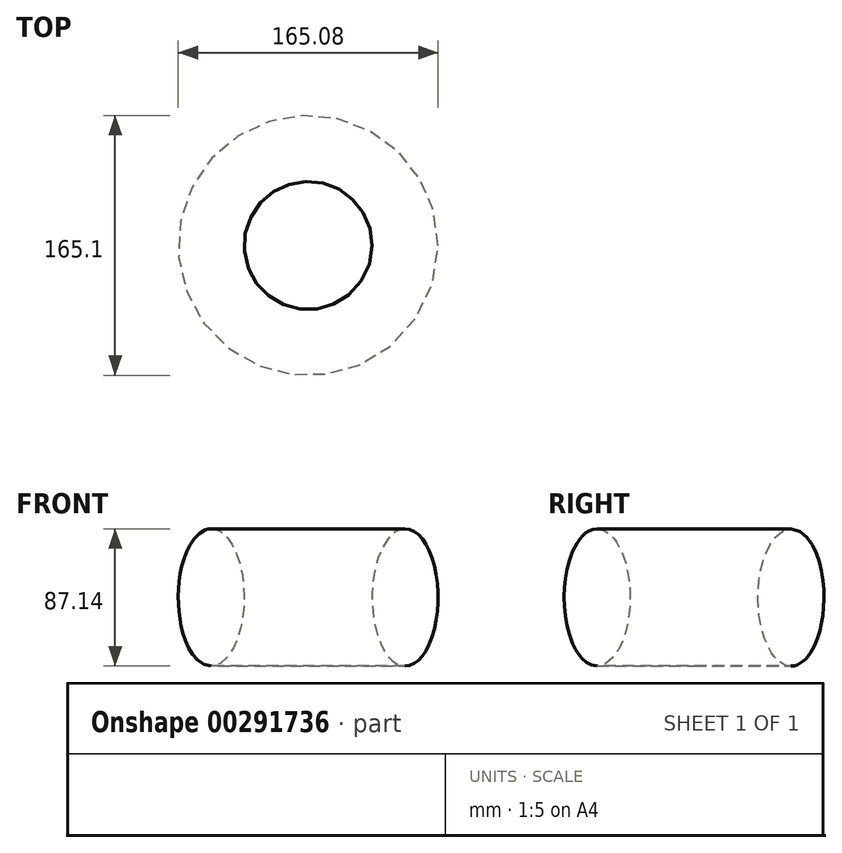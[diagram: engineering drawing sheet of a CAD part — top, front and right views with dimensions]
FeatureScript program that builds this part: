
annotation { "Feature Type Name" : "Feature", "Feature Type Description" : "" }
export const myFeature = defineFeature(function(context is Context, id is Id, definition is map)
    precondition{}
    {
        {
            var Q0;
            Q0=qCreatedBy(makeId("Front.planeOp"),FACE);
            var sketch = newSketch(context, id + "F0", { "sketchPlane" : qUnion([Q0])});
            skEllipse(sketch, "E0", {"center": v(0, 0) * mm, "majorRadius": 43.57 * mm, "minorRadius": 20.95 * mm, "majorAxis": v(0, -1)});
            skLineSegment(sketch, "E1", {"start": v(0, 43.57) * mm, "end": v(0, -43.57) * mm});
            skSolve(sketch);
        }
        {
            var Q0;
            Q0=qCreatedBy(makeId("Front.planeOp"),FACE);
            var sketch = newSketch(context, id + "F1", { "sketchPlane" : qUnion([Q0])});
            skLineSegment(sketch, "E2", {"start": v(-61.6, 59.43) * mm, "end": v(-61.6, -64.73) * mm});
            skSolve(sketch);
        }
        {
            var Q0;
            {var subQ0=sQuery(id+"F0.wireOp",EDGE,"E1");Q0=makeQuery(id+"F0.imprint","IMPRINT",FACE,{"disambiguationData":[TD([[makeQuery(id+"F0.imprint","IMPRINT",EDGE,{"derivedFrom":subQ0}),1.0]])]});}
            var Q1;
            {var subQ0=sQuery(id+"F0.wireOp",EDGE,"E1");Q1=makeQuery(id+"F0.imprint","IMPRINT",FACE,{"disambiguationData":[TD([[makeQuery(id+"F0.imprint","IMPRINT",EDGE,{"derivedFrom":subQ0}),-1.0]])]});}
            var Q2;
            Q2=sQuery(id+"F1.wireOp",EDGE,"E2");
            revolve(context, id + "F2", {"entities" : qUnion([Q0, Q1]), "axis" : qUnion([Q2]), "revolveType" : RevolveType.FULL});
        }
    });
